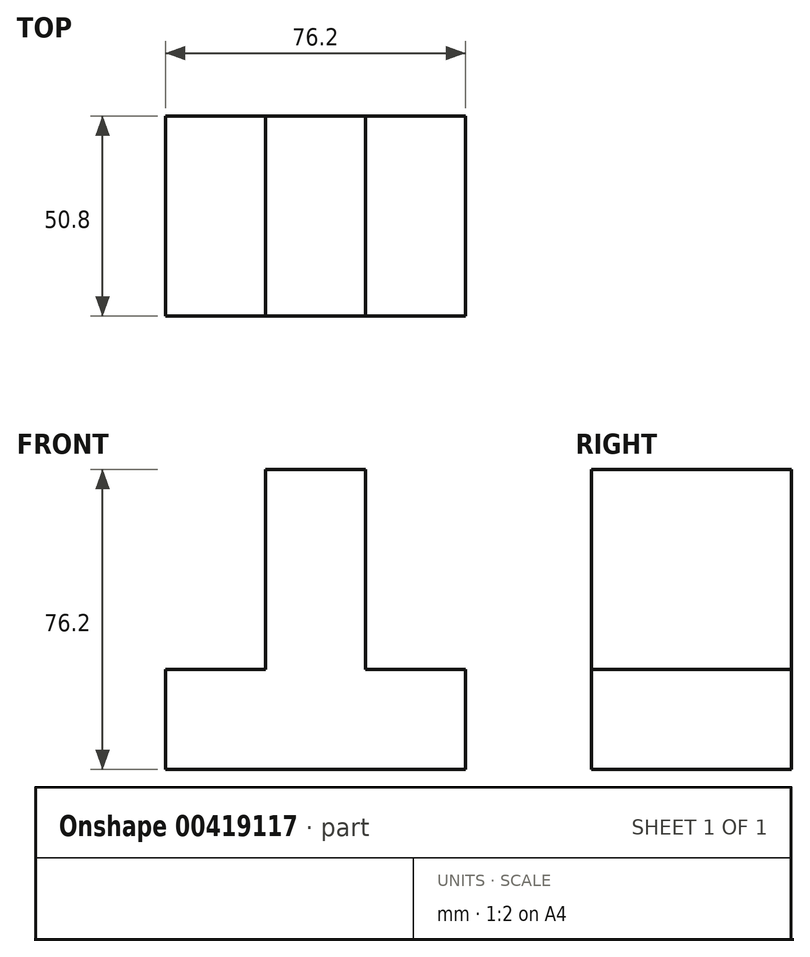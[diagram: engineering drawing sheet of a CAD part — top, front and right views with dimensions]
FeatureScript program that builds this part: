
annotation { "Feature Type Name" : "Feature", "Feature Type Description" : "" }
export const myFeature = defineFeature(function(context is Context, id is Id, definition is map)
    precondition{}
    {
        {
            var Q0;
            Q0=qCreatedBy(makeId("Front.planeOp"),FACE);
            var sketch = newSketch(context, id + "F0", { "sketchPlane" : qUnion([Q0])});
            skLineSegment(sketch, "E0", {"start": v(0, 0) * mm, "end": v(-76.2, 0) * mm});
            skLineSegment(sketch, "E1", {"start": v(0, 0) * mm, "end": v(0, 25.4) * mm});
            skLineSegment(sketch, "E2", {"start": v(-76.2, 0) * mm, "end": v(-76.2, 25.4) * mm});
            skLineSegment(sketch, "E3", {"start": v(0, 25.4) * mm, "end": v(-25.4, 25.4) * mm});
            skLineSegment(sketch, "E4", {"start": v(-76.2, 25.4) * mm, "end": v(-50.8, 25.4) * mm});
            skLineSegment(sketch, "E5", {"start": v(-50.8, 25.4) * mm, "end": v(-50.8, 76.2) * mm});
            skLineSegment(sketch, "E6", {"start": v(-25.4, 25.4) * mm, "end": v(-25.4, 76.2) * mm});
            skLineSegment(sketch, "E7", {"start": v(-50.8, 76.2) * mm, "end": v(-25.4, 76.2) * mm});
            skSolve(sketch);
        }
        {
            var Q0;
            Q0=makeQuery(id+"F0.imprint","IMPRINT",FACE,{"disambiguationData":[TD([[makeQuery(id+"F0.imprint","IMPRINT",EDGE,{"derivedFrom":sQuery(id+"F0.wireOp",EDGE,"E0")}),-1.0]])]});
            extrude(context, id + "F1", {"entities" : qUnion([Q0]), "depth" : 50.8 * mm});
        }
    });
